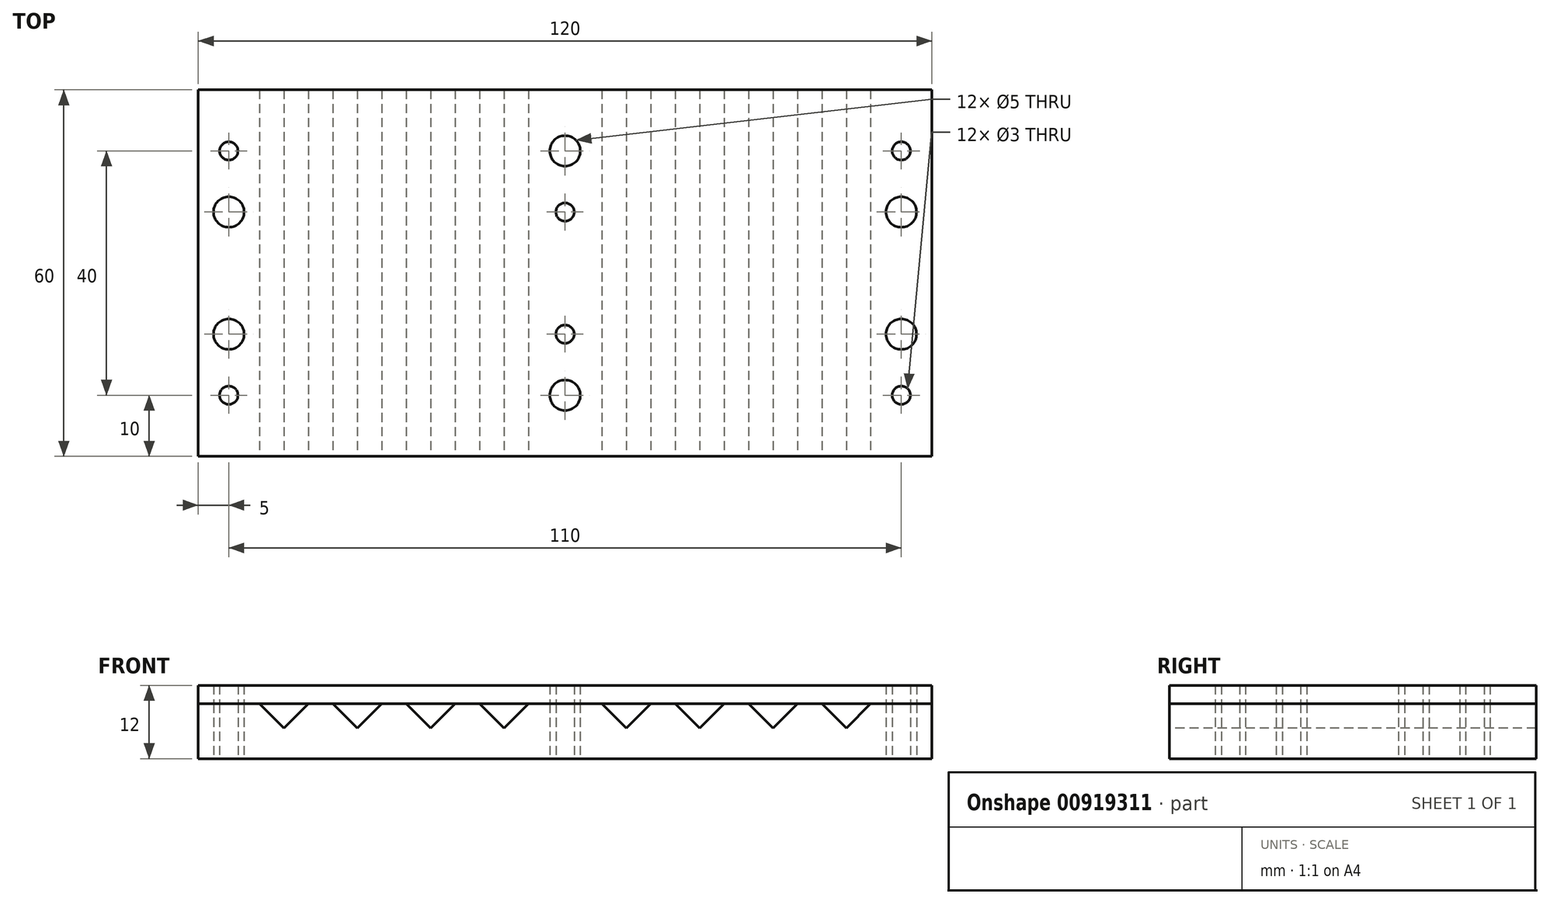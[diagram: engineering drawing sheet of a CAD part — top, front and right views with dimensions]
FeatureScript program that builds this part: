
annotation { "Feature Type Name" : "Feature", "Feature Type Description" : "" }
export const myFeature = defineFeature(function(context is Context, id is Id, definition is map)
    precondition{}
    {
        {
            var Q0;
            Q0=qCreatedBy(makeId("Top.planeOp"),FACE);
            var sketch = newSketch(context, id + "F0", { "sketchPlane" : qUnion([Q0])});
            skPoint(sketch, "E0.middle", {"position": v(0, 0) * mm});
            skLineSegment(sketch, "E1.bottom", {"start": v(0, 0) * mm, "end": v(120, 0) * mm});
            skLineSegment(sketch, "E1.top", {"start": v(0, 60) * mm, "end": v(120, 60) * mm});
            skLineSegment(sketch, "E1.left", {"start": v(0, 0) * mm, "end": v(0, 60) * mm});
            skLineSegment(sketch, "E1.right", {"start": v(120, 0) * mm, "end": v(120, 60) * mm});
            skLineSegment(sketch, "E2", {"start": v(110, 60) * mm, "end": v(110, 0) * mm, "construction": true});
            skLineSegment(sketch, "E3", {"start": v(10, 60) * mm, "end": v(10, 0) * mm, "construction": true});
            skLineSegment(sketch, "E4", {"start": v(5, 60) * mm, "end": v(5, 0) * mm, "construction": true});
            skLineSegment(sketch, "E5", {"start": v(115, 60) * mm, "end": v(115, 0) * mm, "construction": true});
            skPoint(sketch, "E6", {"position": v(5, 40) * mm});
            skPoint(sketch, "E7", {"position": v(5, 20) * mm});
            skPoint(sketch, "E8", {"position": v(115, 40) * mm});
            skPoint(sketch, "E9", {"position": v(115, 20) * mm});
            skCircle(sketch, "E10", {"center": v(5, 40) * mm, "radius": 1.5 * mm, "construction": true});
            skCircle(sketch, "E11", {"center": v(5, 20) * mm, "radius": 1.5 * mm, "construction": true});
            skCircle(sketch, "E12", {"center": v(115, 40) * mm, "radius": 1.5 * mm, "construction": true});
            skCircle(sketch, "E13", {"center": v(115, 20) * mm, "radius": 1.5 * mm, "construction": true});
            skLineSegment(sketch, "E14", {"start": v(60, 60) * mm, "end": v(60, 0) * mm, "construction": true});
            skPoint(sketch, "E15", {"position": v(5, 50) * mm});
            skPoint(sketch, "E16", {"position": v(5, 10) * mm});
            skPoint(sketch, "E17", {"position": v(60, 50) * mm});
            skPoint(sketch, "E18", {"position": v(60, 20) * mm});
            skPoint(sketch, "E19", {"position": v(60, 10) * mm});
            skPoint(sketch, "E20", {"position": v(60, 40) * mm});
            skPoint(sketch, "E21", {"position": v(115, 50) * mm});
            skPoint(sketch, "E22", {"position": v(115, 10) * mm});
            skSolve(sketch);
        }
        {
            var Q0;
            Q0=makeQuery(id+"F0.imprint","IMPRINT",FACE,{"disambiguationData":[TD([[makeQuery(id+"F0.imprint","IMPRINT",EDGE,{"derivedFrom":sQuery(id+"F0.wireOp",EDGE,"E1.bottom")}),1.0]])]});
            extrude(context, id + "F1", {"entities" : qUnion([Q0]), "depth" : 5 * mm, "offsetDistance" : 25 * mm});
        }
        {
            var Q0;
            Q0=makeQuery(id+"F1.opExtrude","SWEPT_FACE",FACE,{"disambiguationData":[OSD([sQuery(id+"F0.wireOp",EDGE,"E1.bottom")])]});
            var sketch = newSketch(context, id + "F2", { "sketchPlane" : qUnion([Q0])});
            skPoint(sketch, "E23", {"position": v(10, 0) * mm});
            skLineSegment(sketch, "E24", {"start": v(0, 0) * mm, "end": v(10, 0) * mm});
            skLineSegment(sketch, "E25", {"start": v(10, 0) * mm, "end": v(10, 5) * mm, "construction": true});
            skLineSegment(sketch, "E26", {"start": v(10, 5) * mm, "end": v(10, 9) * mm, "construction": true});
            skLineSegment(sketch, "E27", {"start": v(10, 5) * mm, "end": v(14, 5) * mm, "construction": true});
            skLineSegment(sketch, "E28", {"start": v(10, 9) * mm, "end": v(14, 5) * mm});
            skLineSegment(sketch, "E29", {"start": v(14, 5) * mm, "end": v(18, 5) * mm, "construction": true});
            skLineSegment(sketch, "E30", {"start": v(18, 5) * mm, "end": v(18, 9) * mm, "construction": true});
            skLineSegment(sketch, "E31", {"start": v(14, 5) * mm, "end": v(18, 9) * mm});
            skLineSegment(sketch, "E32.1.0.0", {"start": v(26, 5) * mm, "end": v(30, 9) * mm});
            skLineSegment(sketch, "E32.1.0.1", {"start": v(22, 9) * mm, "end": v(26, 5) * mm});
            skLineSegment(sketch, "E32.2.0.0", {"start": v(38, 5) * mm, "end": v(42, 9) * mm});
            skLineSegment(sketch, "E32.2.0.1", {"start": v(34, 9) * mm, "end": v(38, 5) * mm});
            skLineSegment(sketch, "E32.direction1", {"start": v(14, 5) * mm, "end": v(26, 5) * mm, "construction": true});
            skLineSegment(sketch, "E33.0.3.0", {"start": v(50, 5) * mm, "end": v(54, 9) * mm});
            skLineSegment(sketch, "E33.3.3.0", {"start": v(46, 9) * mm, "end": v(50, 5) * mm});
            skLineSegment(sketch, "E34.1.0.0", {"start": v(66, 9) * mm, "end": v(70, 5) * mm});
            skLineSegment(sketch, "E34.1.0.1", {"start": v(70, 5) * mm, "end": v(74, 9) * mm});
            skLineSegment(sketch, "E34.1.0.2", {"start": v(78, 9) * mm, "end": v(82, 5) * mm});
            skLineSegment(sketch, "E34.1.0.3", {"start": v(82, 5) * mm, "end": v(86, 9) * mm});
            skLineSegment(sketch, "E34.1.0.4", {"start": v(90, 9) * mm, "end": v(94, 5) * mm});
            skLineSegment(sketch, "E34.1.0.5", {"start": v(94, 5) * mm, "end": v(98, 9) * mm});
            skLineSegment(sketch, "E34.1.0.6", {"start": v(102, 9) * mm, "end": v(106, 5) * mm});
            skLineSegment(sketch, "E34.1.0.7", {"start": v(106, 5) * mm, "end": v(110, 9) * mm});
            skLineSegment(sketch, "E34.direction1", {"start": v(14, 5) * mm, "end": v(70, 5) * mm, "construction": true});
            skLineSegment(sketch, "E35", {"start": v(18, 9) * mm, "end": v(22, 9) * mm});
            skLineSegment(sketch, "E36", {"start": v(30, 9) * mm, "end": v(34, 9) * mm});
            skLineSegment(sketch, "E37", {"start": v(42, 9) * mm, "end": v(46, 9) * mm});
            skLineSegment(sketch, "E38", {"start": v(54, 9) * mm, "end": v(66, 9) * mm});
            skLineSegment(sketch, "E39", {"start": v(74, 9) * mm, "end": v(78, 9) * mm});
            skLineSegment(sketch, "E40", {"start": v(86, 9) * mm, "end": v(90, 9) * mm});
            skLineSegment(sketch, "E41", {"start": v(98, 9) * mm, "end": v(102, 9) * mm});
            skLineSegment(sketch, "E42", {"start": v(0, 5) * mm, "end": v(0, 9) * mm});
            skLineSegment(sketch, "E43", {"start": v(0, 9) * mm, "end": v(10, 9) * mm});
            skLineSegment(sketch, "E44", {"start": v(120, 5) * mm, "end": v(120, 9) * mm});
            skLineSegment(sketch, "E45", {"start": v(110, 9) * mm, "end": v(120, 9) * mm});
            skSolve(sketch);
        }
        {
            var Q0;
            {var subQ0=sQuery(id+"F2.wireOp",EDGE,"E34.1.0.7");Q0=makeQuery(id+"F2.imprint","IMPRINT",FACE,{"disambiguationData":[TD([[makeQuery(id+"F2.imprint","IMPRINT",EDGE,{"derivedFrom":subQ0}),-1.0]])]});}
            var Q1;
            {var subQ0=sQuery(id+"F2.wireOp",EDGE,"E34.1.0.5");Q1=makeQuery(id+"F2.imprint","IMPRINT",FACE,{"disambiguationData":[TD([[makeQuery(id+"F2.imprint","IMPRINT",EDGE,{"derivedFrom":subQ0}),-1.0]])]});}
            var Q2;
            {var subQ0=sQuery(id+"F2.wireOp",EDGE,"E34.1.0.3");Q2=makeQuery(id+"F2.imprint","IMPRINT",FACE,{"disambiguationData":[TD([[makeQuery(id+"F2.imprint","IMPRINT",EDGE,{"derivedFrom":subQ0}),-1.0]])]});}
            var Q3;
            {var subQ0=sQuery(id+"F2.wireOp",EDGE,"E34.1.0.1");Q3=makeQuery(id+"F2.imprint","IMPRINT",FACE,{"disambiguationData":[TD([[makeQuery(id+"F2.imprint","IMPRINT",EDGE,{"derivedFrom":subQ0}),-1.0]])]});}
            var Q4;
            {var subQ0=sQuery(id+"F2.wireOp",EDGE,"E33.0.3.0");Q4=makeQuery(id+"F2.imprint","IMPRINT",FACE,{"disambiguationData":[TD([[makeQuery(id+"F2.imprint","IMPRINT",EDGE,{"derivedFrom":subQ0}),-1.0]])]});}
            var Q5;
            {var subQ0=sQuery(id+"F2.wireOp",EDGE,"E32.2.0.0");Q5=makeQuery(id+"F2.imprint","IMPRINT",FACE,{"disambiguationData":[TD([[makeQuery(id+"F2.imprint","IMPRINT",EDGE,{"derivedFrom":subQ0}),-1.0]])]});}
            var Q6;
            {var subQ0=sQuery(id+"F2.wireOp",EDGE,"E32.1.0.0");Q6=makeQuery(id+"F2.imprint","IMPRINT",FACE,{"disambiguationData":[TD([[makeQuery(id+"F2.imprint","IMPRINT",EDGE,{"derivedFrom":subQ0}),-1.0]])]});}
            var Q7;
            {var subQ0=sQuery(id+"F2.wireOp",EDGE,"E31");Q7=makeQuery(id+"F2.imprint","IMPRINT",FACE,{"disambiguationData":[TD([[makeQuery(id+"F2.imprint","IMPRINT",EDGE,{"derivedFrom":subQ0}),-1.0]])]});}
            var Q8;
            {var subQ0=sQuery(id+"F2.wireOp",EDGE,"E28");Q8=makeQuery(id+"F2.imprint","IMPRINT",FACE,{"disambiguationData":[TD([[makeQuery(id+"F2.imprint","IMPRINT",EDGE,{"derivedFrom":subQ0}),-1.0]])]});}
            extrude(context, id + "F3", {"entities" : qUnion([Q0, Q1, Q2, Q3, Q4, Q5, Q6, Q7, Q8]), "operationType" : NewBodyOperationType.ADD, "oppositeDirection" : true, "depth" : 60 * mm, "offsetDistance" : 25 * mm});
        }
        {
            var Q0;
            Q0=sQuery(id+"F0.wireOp",VERTEX,"E9");
            var Q1;
            Q1=sQuery(id+"F0.wireOp",VERTEX,"E8");
            var Q2;
            Q2=sQuery(id+"F0.wireOp",VERTEX,"E7");
            var Q3;
            Q3=sQuery(id+"F0.wireOp",VERTEX,"E6");
            var Q4;
            Q4=makeQuery(id+"F1.opExtrude","SWEPT_BODY",BODY,{"disambiguationData":[OSD([sQuery(id+"F0.wireOp",EDGE,"E1.bottom"),sQuery(id+"F0.wireOp",EDGE,"E1.top"),sQuery(id+"F0.wireOp",EDGE,"E1.left"),sQuery(id+"F0.wireOp",EDGE,"E1.right")])]});
            hole(context, id + "F4", {"style" : HoleStyle.SIMPLE, "endStyle" : HoleEndStyle.THROUGH, "oppositeDirection" : true, "holeDiameter" : 5 * mm, "majorDiameter" : 5 * mm, "isTappedThrough" : true, "tappedDepth" : 12 * mm, "tapClearance" : 3, "locations" : qUnion([Q0, Q1, Q2, Q3]), "scope" : qUnion([Q4])});
        }
        {
            var Q0;
            Q0=sQuery(id+"F0.wireOp",VERTEX,"E17");
            var Q1;
            Q1=sQuery(id+"F0.wireOp",VERTEX,"E19");
            var Q2;
            Q2=makeQuery(id+"F1.opExtrude","SWEPT_BODY",BODY,{"disambiguationData":[OSD([sQuery(id+"F0.wireOp",EDGE,"E1.bottom"),sQuery(id+"F0.wireOp",EDGE,"E1.top"),sQuery(id+"F0.wireOp",EDGE,"E1.left"),sQuery(id+"F0.wireOp",EDGE,"E1.right")])]});
            hole(context, id + "F5", {"style" : HoleStyle.SIMPLE, "endStyle" : HoleEndStyle.THROUGH, "oppositeDirection" : true, "holeDiameter" : 5 * mm, "majorDiameter" : 5 * mm, "isTappedThrough" : true, "tappedDepth" : 12 * mm, "tapClearance" : 3, "locations" : qUnion([Q0, Q1]), "scope" : qUnion([Q2])});
        }
        {
            var Q0;
            Q0=sQuery(id+"F0.wireOp",VERTEX,"E15");
            var Q1;
            Q1=sQuery(id+"F0.wireOp",VERTEX,"E16");
            var Q2;
            Q2=sQuery(id+"F0.wireOp",VERTEX,"E20");
            var Q3;
            Q3=sQuery(id+"F0.wireOp",VERTEX,"E18");
            var Q4;
            Q4=sQuery(id+"F0.wireOp",VERTEX,"E22");
            var Q5;
            Q5=sQuery(id+"F0.wireOp",VERTEX,"E21");
            var Q6;
            Q6=makeQuery(id+"F1.opExtrude","SWEPT_BODY",BODY,{"disambiguationData":[OSD([sQuery(id+"F0.wireOp",EDGE,"E1.bottom"),sQuery(id+"F0.wireOp",EDGE,"E1.top"),sQuery(id+"F0.wireOp",EDGE,"E1.left"),sQuery(id+"F0.wireOp",EDGE,"E1.right")])]});
            hole(context, id + "F6", {"style" : HoleStyle.SIMPLE, "endStyle" : HoleEndStyle.THROUGH, "oppositeDirection" : true, "holeDiameter" : 3 * mm, "majorDiameter" : 5 * mm, "isTappedThrough" : true, "tappedDepth" : 12 * mm, "tapClearance" : 3, "locations" : qUnion([Q0, Q1, Q2, Q3, Q4, Q5]), "scope" : qUnion([Q6])});
        }
        {
            var Q0;
            Q0=makeQuery(id+"F3.opExtrude","SWEPT_FACE",FACE,{"disambiguationData":[OSD([sQuery(id+"F2.wireOp",EDGE,"E38")])]});
            var sketch = newSketch(context, id + "F7", { "sketchPlane" : qUnion([Q0])});
            skLineSegment(sketch, "E46.bottom", {"start": v(0, 0) * mm, "end": v(120, 0) * mm});
            skLineSegment(sketch, "E46.top", {"start": v(0, 60) * mm, "end": v(120, 60) * mm});
            skLineSegment(sketch, "E46.left", {"start": v(0, 0) * mm, "end": v(0, 60) * mm});
            skLineSegment(sketch, "E46.right", {"start": v(120, 0) * mm, "end": v(120, 60) * mm});
            skSolve(sketch);
        }
        {
            var Q0;
            {var subQ2=sQuery(id+"F7.wireOp",EDGE,"E46.left");Q0=makeQuery(id+"F7.imprint","IMPRINT",FACE,{"disambiguationData":[TD([[makeQuery(id+"F7.imprint","IMPRINT",EDGE,{"derivedFrom":subQ2}),-1.0]])]});}
            var Q1;
            {var subQ2=sQuery(id+"F7.wireOp",EDGE,"E46.right");Q1=makeQuery(id+"F7.imprint","IMPRINT",FACE,{"disambiguationData":[TD([[makeQuery(id+"F7.imprint","IMPRINT",EDGE,{"derivedFrom":subQ2}),1.0]])]});}
            var Q2;
            {var subQ0=sQuery(id+"F2.wireOp",EDGE,"E38");var subQ1=makeQuery(id+"F3.opExtrude","SWEPT_EDGE",EDGE,{"disambiguationData":[OSD([sQuery(id+"F2.wireOp",EDGE,"E33.0.3.0"),subQ0])]});Q2=makeQuery(id+"F7.imprint","IMPRINT",FACE,{"disambiguationData":[TD([[makeQuery(id+"F7.imprint","IMPRINT",EDGE,{"derivedFrom":subQ1}),1.0]])]});}
            var Q3;
            Q3=makeQuery(id+"F7.imprint","IMPRINT",FACE,{"disambiguationData":[TD([[makeQuery(id+"F7.imprint","IMPRINT",EDGE,{"derivedFrom":makeQuery(id+"F5.hole-0.boolean.opBoolean","INTERSECT",EDGE,{"derivedFrom":[makeQuery(id+"F3.opExtrude","SWEPT_FACE",FACE,{"disambiguationData":[OSD([sQuery(id+"F2.wireOp",EDGE,"E38")])]}),makeQuery(id+"F5.hole-0.opRevolve","SWEPT_FACE",FACE,{"disambiguationData":[OSD([sQuery(id+"F5.hole-0.sketch.wireOp",EDGE,"core_line_2")])]})]})}),1.0]])]});
            var Q4;
            Q4=makeQuery(id+"F7.imprint","IMPRINT",FACE,{"disambiguationData":[TD([[makeQuery(id+"F7.imprint","IMPRINT",EDGE,{"derivedFrom":makeQuery(id+"F6.hole-2.boolean.opBoolean","INTERSECT",EDGE,{"derivedFrom":[makeQuery(id+"F3.opExtrude","SWEPT_FACE",FACE,{"disambiguationData":[OSD([sQuery(id+"F2.wireOp",EDGE,"E38")])]}),makeQuery(id+"F6.hole-2.opRevolve","SWEPT_FACE",FACE,{"disambiguationData":[OSD([sQuery(id+"F6.hole-2.sketch.wireOp",EDGE,"core_line_2")])]})]})}),1.0]])]});
            var Q5;
            Q5=makeQuery(id+"F7.imprint","IMPRINT",FACE,{"disambiguationData":[TD([[makeQuery(id+"F7.imprint","IMPRINT",EDGE,{"derivedFrom":makeQuery(id+"F5.hole-1.boolean.opBoolean","INTERSECT",EDGE,{"derivedFrom":[makeQuery(id+"F3.opExtrude","SWEPT_FACE",FACE,{"disambiguationData":[OSD([sQuery(id+"F2.wireOp",EDGE,"E38")])]}),makeQuery(id+"F5.hole-1.opRevolve","SWEPT_FACE",FACE,{"disambiguationData":[OSD([sQuery(id+"F5.hole-1.sketch.wireOp",EDGE,"core_line_2")])]})]})}),1.0]])]});
            var Q6;
            Q6=makeQuery(id+"F7.imprint","IMPRINT",FACE,{"disambiguationData":[TD([[makeQuery(id+"F7.imprint","IMPRINT",EDGE,{"derivedFrom":makeQuery(id+"F6.hole-3.boolean.opBoolean","INTERSECT",EDGE,{"derivedFrom":[makeQuery(id+"F3.opExtrude","SWEPT_FACE",FACE,{"disambiguationData":[OSD([sQuery(id+"F2.wireOp",EDGE,"E38")])]}),makeQuery(id+"F6.hole-3.opRevolve","SWEPT_FACE",FACE,{"disambiguationData":[OSD([sQuery(id+"F6.hole-3.sketch.wireOp",EDGE,"core_line_2")])]})]})}),1.0]])]});
            extrude(context, id + "F8", {"entities" : qUnion([Q0, Q1, Q2, Q3, Q4, Q5, Q6]), "depth" : 3 * mm, "offsetDistance" : 25 * mm});
        }
        {
            var Q0;
            Q0=sQuery(id+"F0.wireOp",VERTEX,"E22");
            var Q1;
            Q1=sQuery(id+"F0.wireOp",VERTEX,"E21");
            var Q2;
            Q2=sQuery(id+"F0.wireOp",VERTEX,"E20");
            var Q3;
            Q3=sQuery(id+"F0.wireOp",VERTEX,"E18");
            var Q4;
            Q4=sQuery(id+"F0.wireOp",VERTEX,"E16");
            var Q5;
            Q5=sQuery(id+"F0.wireOp",VERTEX,"E15");
            var Q6;
            Q6=makeQuery(id+"F8.opExtrude","SWEPT_BODY",BODY,{"disambiguationData":[OSD([sQuery(id+"F7.wireOp",EDGE,"E46.bottom"),sQuery(id+"F7.wireOp",EDGE,"E46.top"),sQuery(id+"F7.wireOp",EDGE,"E46.left"),sQuery(id+"F7.wireOp",EDGE,"E46.right")])]});
            hole(context, id + "F9", {"style" : HoleStyle.SIMPLE, "endStyle" : HoleEndStyle.THROUGH, "oppositeDirection" : true, "holeDiameter" : 3 * mm, "majorDiameter" : 5 * mm, "isTappedThrough" : true, "tappedDepth" : 12 * mm, "tapClearance" : 3, "locations" : qUnion([Q0, Q1, Q2, Q3, Q4, Q5]), "scope" : qUnion([Q6])});
        }
        {
            var Q0;
            Q0=sQuery(id+"F0.wireOp",VERTEX,"E13.center");
            var Q1;
            Q1=sQuery(id+"F0.wireOp",VERTEX,"E12.center");
            var Q2;
            Q2=sQuery(id+"F0.wireOp",VERTEX,"E17");
            var Q3;
            Q3=sQuery(id+"F0.wireOp",VERTEX,"E19");
            var Q4;
            Q4=sQuery(id+"F0.wireOp",VERTEX,"E7");
            var Q5;
            Q5=sQuery(id+"F0.wireOp",VERTEX,"E6");
            var Q6;
            Q6=makeQuery(id+"F8.opExtrude","SWEPT_BODY",BODY,{"disambiguationData":[OSD([sQuery(id+"F7.wireOp",EDGE,"E46.bottom"),sQuery(id+"F7.wireOp",EDGE,"E46.top"),sQuery(id+"F7.wireOp",EDGE,"E46.left"),sQuery(id+"F7.wireOp",EDGE,"E46.right")])]});
            hole(context, id + "F10", {"style" : HoleStyle.SIMPLE, "endStyle" : HoleEndStyle.THROUGH, "oppositeDirection" : true, "holeDiameter" : 5 * mm, "majorDiameter" : 5 * mm, "isTappedThrough" : true, "tappedDepth" : 12 * mm, "tapClearance" : 3, "locations" : qUnion([Q0, Q1, Q2, Q3, Q4, Q5]), "scope" : qUnion([Q6])});
        }
    });
